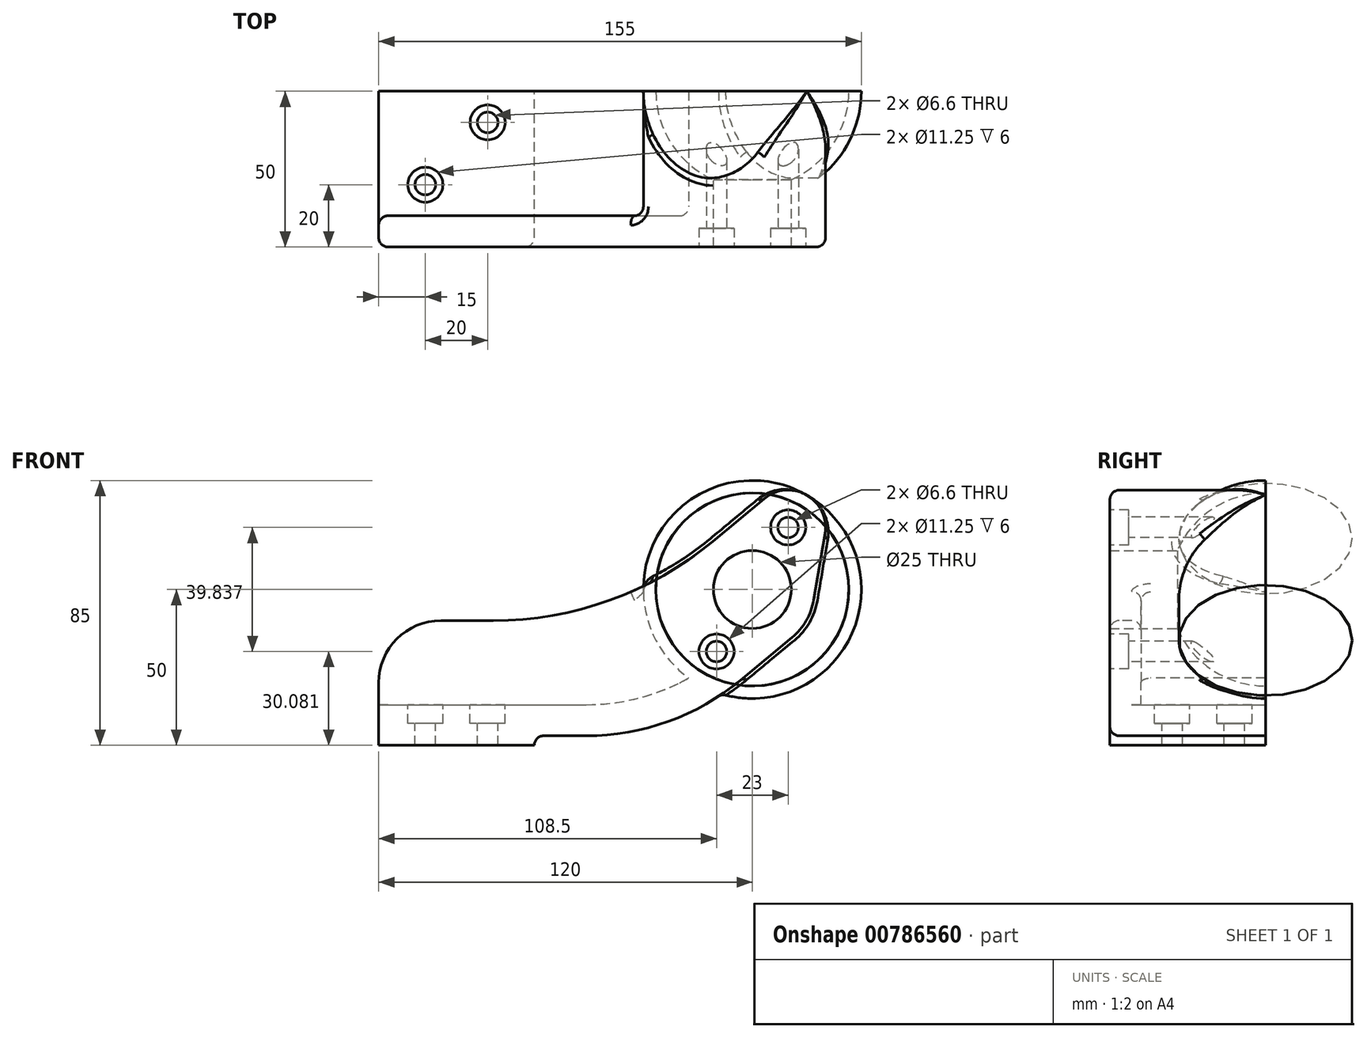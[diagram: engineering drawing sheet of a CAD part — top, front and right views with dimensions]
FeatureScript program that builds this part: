
annotation { "Feature Type Name" : "Feature", "Feature Type Description" : "" }
export const myFeature = defineFeature(function(context is Context, id is Id, definition is map)
    precondition{}
    {
        {
            var Q0;
            Q0=qCreatedBy(makeId("Front.planeOp"),FACE);
            var sketch = newSketch(context, id + "F0", { "sketchPlane" : qUnion([Q0])});
            skCircle(sketch, "E0", {"center": v(120, 50) * mm, "radius": 35 * mm});
            skCircle(sketch, "E1", {"center": v(120, 50) * mm, "radius": 12.5 * mm});
            skLineSegment(sketch, "E2", {"start": v(102.5, 19.69) * mm, "end": v(137.5, 80.31) * mm, "construction": true});
            skArc(sketch, "E3", {"start": v(122.23, 62.3) * mm, "mid": v(125.5, 59.53) * mm, "end": v(129.54, 58.08) * mm, "construction": true});
            skArc(sketch, "E4", {"start": v(96.67, 32.1) * mm, "mid": v(102.5, 19.69) * mm, "end": v(116.16, 20.84) * mm});
            skArc(sketch, "E5", {"start": v(107.24, 65.4) * mm, "mid": v(102.68, 60) * mm, "end": v(100.28, 53.35) * mm});
            skLineSegment(sketch, "E6", {"start": v(0, 0) * mm, "end": v(50, 0) * mm});
            skLineSegment(sketch, "E7", {"start": v(50, 0) * mm, "end": v(50, 3) * mm});
            skLineSegment(sketch, "E8", {"start": v(50, 3) * mm, "end": v(66.66, 3) * mm});
            skLineSegment(sketch, "E9", {"start": v(0, 0) * mm, "end": v(0, 40) * mm});
            skLineSegment(sketch, "E10", {"start": v(0, 40) * mm, "end": v(86.46, 40) * mm});
            skLineSegment(sketch, "E11", {"start": v(139.72, 46.65) * mm, "end": v(143.33, 67.9) * mm});
            skLineSegment(sketch, "E12", {"start": v(107.24, 65.4) * mm, "end": v(123.84, 79.16) * mm});
            skLineSegment(sketch, "E13", {"start": v(100.28, 53.35) * mm, "end": v(96.67, 32.1) * mm});
            skLineSegment(sketch, "E14", {"start": v(132.76, 34.6) * mm, "end": v(116.16, 20.84) * mm});
            skArc(sketch, "E15.trimOffspring", {"start": v(143.33, 67.9) * mm, "mid": v(137.5, 80.31) * mm, "end": v(123.84, 79.16) * mm});
            skArc(sketch, "E16.trimOffspring", {"start": v(117.77, 37.7) * mm, "mid": v(114.5, 40.47) * mm, "end": v(110.46, 41.92) * mm, "construction": true});
            skArc(sketch, "E17.trimOffspring", {"start": v(132.76, 34.6) * mm, "mid": v(137.32, 40) * mm, "end": v(139.72, 46.65) * mm});
            skArc(sketch, "E18", {"start": v(66.66, 3) * mm, "mid": v(92.97, 7.6) * mm, "end": v(116.16, 20.84) * mm});
            skArc(sketch, "E19.0", {"start": v(66.66, 13) * mm, "mid": v(83.84, 15.22) * mm, "end": v(99.88, 21.73) * mm});
            skLineSegment(sketch, "E20", {"start": v(0, 13) * mm, "end": v(66.66, 13) * mm});
            skSolve(sketch);
        }
        {
            var Q0;
            Q0=makeQuery(id+"F0.imprint","IMPRINT",FACE,{"disambiguationData":[TD([[makeQuery(id+"F0.imprint","IMPRINT",EDGE,{"derivedFrom":sQuery(id+"F0.wireOp",EDGE,"E5")}),-1.0]])]});
            var sketch = newSketch(context, id + "F1", { "sketchPlane" : qUnion([Q0])});
            skArc(sketch, "E21.0", {"start": v(119.02, 84.99) * mm, "mid": v(85.01, 49.02) * mm, "end": v(120.98, 15.01) * mm});
            skLineSegment(sketch, "E22", {"start": v(119.02, 84.99) * mm, "end": v(120.98, 15.01) * mm});
            skSolve(sketch);
        }
        {
            var Q0;
            Q0 = qSketchRegion(id + "F1", true);
            var Q1;
            Q1=sQuery(id+"F1.wireOp",EDGE,"E22");
            revolve(context, id + "F2", {"surfaceOperationType" : NewSurfaceOperationType.NEW, "entities" : qUnion([Q0]), "axis" : qUnion([Q1]), "revolveType" : RevolveType.ONE_DIRECTION, "oppositeDirection" : true, "angle" : 180 * degree});
        }
        {
            var Q0;
            {var subQ0=sQuery(id+"F0.wireOp",EDGE,"E19.0");var subQ1=sQuery(id+"F0.wireOp",EDGE,"E0");var subQ2=makeQuery(id+"F0.imprint","INTERSECT",VERTEX,{"derivedFrom":[subQ1,subQ0]});Q0=makeQuery(id+"F0.imprint","IMPRINT",FACE,{"disambiguationData":[TD([[makeQuery(id+"F0.imprint","IMPRINT",EDGE,{"disambiguationData":[TD([[subQ2,-1.0]])],"derivedFrom":subQ1}),1.0]])]});}
            var Q1;
            {var subQ0=sQuery(id+"F0.wireOp",EDGE,"E18");var subQ1=sQuery(id+"F0.wireOp",EDGE,"E0");var subQ2=makeQuery(id+"F0.imprint","INTERSECT",VERTEX,{"derivedFrom":[subQ1,subQ0]});Q1=makeQuery(id+"F0.imprint","IMPRINT",FACE,{"disambiguationData":[TD([[makeQuery(id+"F0.imprint","IMPRINT",EDGE,{"disambiguationData":[TD([[subQ2,1.0]])],"derivedFrom":subQ1}),1.0]])]});}
            var Q2;
            {var subQ0=sQuery(id+"F0.wireOp",EDGE,"E6");Q2=makeQuery(id+"F0.imprint","IMPRINT",FACE,{"disambiguationData":[TD([[makeQuery(id+"F0.imprint","IMPRINT",EDGE,{"derivedFrom":subQ0}),1.0]])]});}
            var Q3;
            Q3=makeQuery(id+"F0.imprint","IMPRINT",FACE,{"disambiguationData":[TD([[makeQuery(id+"F0.imprint","IMPRINT",EDGE,{"derivedFrom":sQuery(id+"F0.wireOp",EDGE,"E1")}),-1.0]])]});
            var Q4;
            Q4=makeQuery(id+"F0.imprint","IMPRINT",FACE,{"disambiguationData":[TD([[makeQuery(id+"F0.imprint","IMPRINT",EDGE,{"derivedFrom":sQuery(id+"F0.wireOp",EDGE,"E1")}),1.0]])]});
            extrude(context, id + "F3", {"entities" : qUnion([Q0, Q1, Q2, Q3, Q4]), "operationType" : NewBodyOperationType.ADD, "depth" : 50 * mm, "offsetDistance" : 25 * mm});
        }
        {
            var Q0;
            {var subQ0=sQuery(id+"F0.wireOp",EDGE,"E20");Q0=makeQuery(id+"FL2OrtGu8nAbXdU_1.boolean.opBoolean","MERGE",FACE,{"derivedFrom":[makeQuery(id+"F3.opExtrude","SWEPT_FACE",FACE,{"disambiguationData":[OSD([subQ0])]}),makeQuery(id+"FL2OrtGu8nAbXdU_1.opExtrude","SWEPT_FACE",FACE,{"disambiguationData":[OSD([sQuery(id+"F0.wireOp",EDGE,"E9"),subQ0])]})]});}
            var sketch = newSketch(context, id + "F4", { "sketchPlane" : qUnion([Q0])});
            skPoint(sketch, "E23", {"position": v(15, -30) * mm});
            skPoint(sketch, "E24", {"position": v(35, -10) * mm});
            skSolve(sketch);
        }
        {
            var Q0;
            Q0=makeQuery(id+"F3.opExtrude","CAP_FACE",FACE,{"disambiguationData":[OSD([sQuery(id+"F0.wireOp",EDGE,"E1"),sQuery(id+"F0.wireOp",EDGE,"E4"),sQuery(id+"F0.wireOp",EDGE,"E5"),sQuery(id+"F0.wireOp",EDGE,"E6"),sQuery(id+"F0.wireOp",EDGE,"E7"),sQuery(id+"F0.wireOp",EDGE,"E8"),sQuery(id+"F0.wireOp",EDGE,"E9"),sQuery(id+"F0.wireOp",EDGE,"E11"),sQuery(id+"F0.wireOp",EDGE,"E12"),sQuery(id+"F0.wireOp",EDGE,"E13"),sQuery(id+"F0.wireOp",EDGE,"E14"),sQuery(id+"F0.wireOp",EDGE,"E15.trimOffspring"),sQuery(id+"F0.wireOp",EDGE,"E17.trimOffspring"),sQuery(id+"F0.wireOp",EDGE,"E18"),sQuery(id+"F0.wireOp",EDGE,"E19.0"),sQuery(id+"F0.wireOp",EDGE,"E20")])],"isStart":false});
            var sketch = newSketch(context, id + "F5", { "sketchPlane" : qUnion([Q0])});
            skCircle(sketch, "E25", {"center": v(120, 50) * mm, "radius": 23 * mm, "construction": true});
            skLineSegment(sketch, "E26", {"start": v(108.5, 30.08) * mm, "end": v(131.5, 69.92) * mm, "construction": true});
            skSolve(sketch);
        }
        {
            var Q0;
            Q0=sQuery(id+"F4.wireOp",VERTEX,"E24");
            var Q1;
            Q1=sQuery(id+"F4.wireOp",VERTEX,"E23");
            var Q2;
            Q2=sQuery(id+"F5.wireOp",VERTEX,"E26.end");
            var Q3;
            Q3=sQuery(id+"F5.wireOp",VERTEX,"E26.start");
            var Q4;
            Q4=makeQuery(id+"F2.opRevolve","SWEPT_BODY",BODY,{"disambiguationData":[OSD([sQuery(id+"F1.wireOp",EDGE,"E21.0"),sQuery(id+"F1.wireOp",EDGE,"E22")])]});
            hole(context, id + "F6", {"style" : HoleStyle.C_BORE, "endStyle" : HoleEndStyle.THROUGH, "standardTappedOrClearance" : lookupTablePath({ "standard" : "ISO", "fit" : "Normal", "size" : "M6", "type" : "Clearance" }), "standardBlindInLast" : lookupTablePath({ "fit" : "Standard", "standard" : "ISO", "size" : "M6", "type" : "Clearance" }), "holeDiameter" : 6.6 * mm, "cBoreDiameter" : 11.25 * mm, "cBoreDepth" : 6 * mm, "majorDiameter" : 5 * mm, "isTappedThrough" : true, "tappedDepth" : 12 * mm, "tapClearance" : 3, "locations" : qUnion([Q0, Q1, Q2, Q3]), "scope" : qUnion([Q4])});
        }
        {
            var Q0;
            Q0=makeQuery(id+"FmB4rHgyCXXtYKF_1.boolean.opBoolean","MERGE",FACE,{"derivedFrom":[makeQuery(id+"F3.boolean.opBoolean","MERGE",FACE,{"derivedFrom":[makeQuery(id+"F2.opRevolve","CAP_FACE",FACE,{"disambiguationData":[OSD([sQuery(id+"F1.wireOp",EDGE,"E21.0"),sQuery(id+"F1.wireOp",EDGE,"E22")])],"isStart":true}),makeQuery(id+"F3.opExtrude","CAP_FACE",FACE,{"disambiguationData":[OSD([sQuery(id+"F0.wireOp",EDGE,"E1"),sQuery(id+"F0.wireOp",EDGE,"E4"),sQuery(id+"F0.wireOp",EDGE,"E5"),sQuery(id+"F0.wireOp",EDGE,"E6"),sQuery(id+"F0.wireOp",EDGE,"E7"),sQuery(id+"F0.wireOp",EDGE,"E8"),sQuery(id+"F0.wireOp",EDGE,"E9"),sQuery(id+"F0.wireOp",EDGE,"E11"),sQuery(id+"F0.wireOp",EDGE,"E12"),sQuery(id+"F0.wireOp",EDGE,"E13"),sQuery(id+"F0.wireOp",EDGE,"E14"),sQuery(id+"F0.wireOp",EDGE,"E15.trimOffspring"),sQuery(id+"F0.wireOp",EDGE,"E17.trimOffspring"),sQuery(id+"F0.wireOp",EDGE,"E18"),sQuery(id+"F0.wireOp",EDGE,"E19.0"),sQuery(id+"F0.wireOp",EDGE,"E20")])],"isStart":true})]}),makeQuery(id+"FmB4rHgyCXXtYKF_1.opExtrude","SWEPT_FACE",FACE,{"disambiguationData":[OSD([sQuery(id+"Fw0tHJBMQvCtHRQ_1.wireOp",EDGE,"a3YMDeG1-MOU3-Fpiz-S6uy-zRs6AQd0MLk7.left")])]})]});
            var sketch = newSketch(context, id + "F7", { "sketchPlane" : qUnion([Q0])});
            skArc(sketch, "E27.0", {"start": v(-131.95, 78.6) * mm, "mid": v(-148.6, 38.05) * mm, "end": v(-108.05, 21.4) * mm});
            skLineSegment(sketch, "E28", {"start": v(-108.05, 21.4) * mm, "end": v(-131.95, 78.6) * mm});
            skSolve(sketch);
        }
        {
            var Q0;
            Q0 = qSketchRegion(id + "F7", true);
            var Q1;
            Q1=sQuery(id+"F7.wireOp",EDGE,"E28");
            revolve(context, id + "F8", {"operationType" : NewBodyOperationType.REMOVE, "surfaceOperationType" : NewSurfaceOperationType.NEW, "entities" : qUnion([Q0]), "axis" : qUnion([Q1]), "revolveType" : RevolveType.FULL, "oppositeDirection" : true});
        }
        {
            var Q0;
            Q0=makeQuery(id+"F0.imprint","IMPRINT",FACE,{"disambiguationData":[TD([[makeQuery(id+"F0.imprint","IMPRINT",EDGE,{"derivedFrom":sQuery(id+"F0.wireOp",EDGE,"E1")}),1.0]])]});
            extrude(context, id + "F9", {"entities" : qUnion([Q0]), "operationType" : NewBodyOperationType.REMOVE, "endBound" : BoundingType.THROUGH_ALL, "depth" : 106.3 * mm, "offsetDistance" : 25 * mm});
        }
        {
            var Q0;
            Q0=makeQuery(id+"F3.opExtrude","CAP_FACE",FACE,{"disambiguationData":[OSD([sQuery(id+"F0.wireOp",EDGE,"E4"),sQuery(id+"F0.wireOp",EDGE,"E5"),sQuery(id+"F0.wireOp",EDGE,"E6"),sQuery(id+"F0.wireOp",EDGE,"E7"),sQuery(id+"F0.wireOp",EDGE,"E8"),sQuery(id+"F0.wireOp",EDGE,"E9"),sQuery(id+"F0.wireOp",EDGE,"E11"),sQuery(id+"F0.wireOp",EDGE,"E12"),sQuery(id+"F0.wireOp",EDGE,"E13"),sQuery(id+"F0.wireOp",EDGE,"E14"),sQuery(id+"F0.wireOp",EDGE,"E15.trimOffspring"),sQuery(id+"F0.wireOp",EDGE,"E17.trimOffspring"),sQuery(id+"F0.wireOp",EDGE,"E18"),sQuery(id+"F0.wireOp",EDGE,"E19.0"),sQuery(id+"F0.wireOp",EDGE,"E20")])],"isStart":false});
            var sketch = newSketch(context, id + "F10", { "sketchPlane" : qUnion([Q0])});
            skLineSegment(sketch, "E29", {"start": v(0, 13) * mm, "end": v(0, 20) * mm});
            skLineSegment(sketch, "E30", {"start": v(20, 40) * mm, "end": v(36.78, 40) * mm});
            skArc(sketch, "E31", {"start": v(36.78, 40) * mm, "mid": v(74.23, 46.54) * mm, "end": v(107.24, 65.4) * mm});
            skPoint(sketch, "E32.visualSharp", {"position": v(0, 40) * mm});
            skArc(sketch, "E32.filletArc", {"start": v(20, 40) * mm, "mid": v(5.86, 34.14) * mm, "end": v(0, 20) * mm});
            skArc(sketch, "E33.0", {"start": v(107.24, 65.4) * mm, "mid": v(102.68, 60) * mm, "end": v(100.28, 53.35) * mm});
            skLineSegment(sketch, "E33.1", {"start": v(100.28, 53.35) * mm, "end": v(96.67, 32.1) * mm});
            skArc(sketch, "E33.2", {"start": v(96.67, 32.1) * mm, "mid": v(97.04, 26.53) * mm, "end": v(99.88, 21.73) * mm});
            skArc(sketch, "E33.3", {"start": v(66.66, 13) * mm, "mid": v(83.84, 15.22) * mm, "end": v(99.88, 21.73) * mm});
            skLineSegment(sketch, "E33.4", {"start": v(0, 13) * mm, "end": v(66.66, 13) * mm});
            skSolve(sketch);
        }
        {
            var Q0;
            Q0=makeQuery(id+"F10.imprint","IMPRINT",FACE,{"disambiguationData":[TD([[makeQuery(id+"F10.imprint","IMPRINT",EDGE,{"derivedFrom":sQuery(id+"F10.wireOp",EDGE,"E29")}),-1.0]])]});
            extrude(context, id + "F11", {"entities" : qUnion([Q0]), "operationType" : NewBodyOperationType.ADD, "oppositeDirection" : true, "depth" : 10 * mm, "offsetDistance" : 25 * mm});
        }
        {
            var Q0;
            Q0=makeQuery(id+"F11.boolean.opBoolean","MERGE",FACE,{"derivedFrom":[makeQuery(id+"F3.opExtrude","CAP_FACE",FACE,{"disambiguationData":[OSD([sQuery(id+"F0.wireOp",EDGE,"E4"),sQuery(id+"F0.wireOp",EDGE,"E5"),sQuery(id+"F0.wireOp",EDGE,"E6"),sQuery(id+"F0.wireOp",EDGE,"E7"),sQuery(id+"F0.wireOp",EDGE,"E8"),sQuery(id+"F0.wireOp",EDGE,"E9"),sQuery(id+"F0.wireOp",EDGE,"E11"),sQuery(id+"F0.wireOp",EDGE,"E12"),sQuery(id+"F0.wireOp",EDGE,"E13"),sQuery(id+"F0.wireOp",EDGE,"E14"),sQuery(id+"F0.wireOp",EDGE,"E15.trimOffspring"),sQuery(id+"F0.wireOp",EDGE,"E17.trimOffspring"),sQuery(id+"F0.wireOp",EDGE,"E18"),sQuery(id+"F0.wireOp",EDGE,"E19.0"),sQuery(id+"F0.wireOp",EDGE,"E20")])],"isStart":false}),makeQuery(id+"F11.opExtrude","CAP_FACE",FACE,{"disambiguationData":[OSD([sQuery(id+"F10.wireOp",EDGE,"E29"),sQuery(id+"F10.wireOp",EDGE,"E30"),sQuery(id+"F10.wireOp",EDGE,"E31"),sQuery(id+"F10.wireOp",EDGE,"E32.filletArc"),sQuery(id+"F10.wireOp",EDGE,"E33.0"),sQuery(id+"F10.wireOp",EDGE,"E33.1"),sQuery(id+"F10.wireOp",EDGE,"E33.2"),sQuery(id+"F10.wireOp",EDGE,"E33.3"),sQuery(id+"F10.wireOp",EDGE,"E33.4")])],"isStart":true})]});
            var sketch = newSketch(context, id + "F12", { "sketchPlane" : qUnion([Q0])});
            skArc(sketch, "E34.0.0", {"start": v(85.02, 51.1) * mm, "mid": v(88.61, 34.5) * mm, "end": v(99.6, 21.57) * mm});
            skArc(sketch, "E34.0.1", {"start": v(99.88, 21.73) * mm, "mid": v(99.74, 21.65) * mm, "end": v(99.6, 21.57) * mm});
            skArc(sketch, "E34.0.2", {"start": v(99.88, 21.73) * mm, "mid": v(97.04, 26.53) * mm, "end": v(96.67, 32.1) * mm});
            skLineSegment(sketch, "E34.0.3", {"start": v(96.67, 32.1) * mm, "end": v(100.28, 53.35) * mm});
            skArc(sketch, "E34.0.4", {"start": v(107.24, 65.4) * mm, "mid": v(102.68, 60) * mm, "end": v(100.28, 53.35) * mm});
            skArc(sketch, "E35.0", {"start": v(85.02, 51.1) * mm, "mid": v(96.56, 57.58) * mm, "end": v(107.24, 65.4) * mm});
            skPoint(sketch, "E34.0.6.start.orphan", {"position": v(123.84, 79.16) * mm});
            skPoint(sketch, "E36.orphan", {"position": v(137.5, 80.31) * mm});
            skSolve(sketch);
        }
        {
            var Q0;
            Q0=makeQuery(id+"F12.imprint","IMPRINT",FACE,{"disambiguationData":[TD([[makeQuery(id+"F12.imprint","IMPRINT",EDGE,{"derivedFrom":sQuery(id+"F12.wireOp",EDGE,"E34.0.0")}),1.0]])]});
            var Q1;
            {var subQ5=sQuery(id+"F0.wireOp",EDGE,"E4");var subQ6=sQuery(id+"F1.wireOp",EDGE,"E21.0");var subQ7=makeQuery(id+"F2.opRevolve","SWEPT_FACE",FACE,{"disambiguationData":[OSD([subQ6])]});Q1=makeQuery(id+"F3.boolean.opBoolean","SPLIT",FACE,{"disambiguationData":[TD([makeQuery(id+"F3.opExtrude","SWEPT_FACE",FACE,{"disambiguationData":[OSD([subQ5])]})])],"derivedFrom":subQ7});}
            extrude(context, id + "F13", {"entities" : qUnion([Q0]), "operationType" : NewBodyOperationType.ADD, "endBound" : BoundingType.UP_TO_SURFACE, "oppositeDirection" : true, "depth" : 21.1 * mm, "endBoundEntityFace" : qUnion([Q1]), "offsetDistance" : 25 * mm});
        }
        {
            var Q0;
            Q0=makeQuery(id+"F13.opExtrude","SWEPT_EDGE",EDGE,{"disambiguationData":[OSD([sQuery(id+"F10.wireOp",EDGE,"E31"),sQuery(id+"F12.wireOp",EDGE,"E34.0.0"),sQuery(id+"F12.wireOp",EDGE,"E35.0")])]});
            var Q1;
            Q1=makeQuery(id+"F11.opExtrude","CAP_EDGE",EDGE,{"disambiguationData":[OSD([sQuery(id+"F10.wireOp",EDGE,"E31")])],"isStart":false});
            var Q2;
            Q2=makeQuery(id+"F13.boolean.opBoolean","INTERSECT",EDGE,{"derivedFrom":[makeQuery(id+"F11.opExtrude","CAP_FACE",FACE,{"disambiguationData":[OSD([sQuery(id+"F10.wireOp",EDGE,"E29"),sQuery(id+"F10.wireOp",EDGE,"E30"),sQuery(id+"F10.wireOp",EDGE,"E31"),sQuery(id+"F10.wireOp",EDGE,"E32.filletArc"),sQuery(id+"F10.wireOp",EDGE,"E33.0"),sQuery(id+"F10.wireOp",EDGE,"E33.1"),sQuery(id+"F10.wireOp",EDGE,"E33.2"),sQuery(id+"F10.wireOp",EDGE,"E33.3"),sQuery(id+"F10.wireOp",EDGE,"E33.4")])],"isStart":false}),makeQuery(id+"F13.opExtrude","SWEPT_FACE",FACE,{"disambiguationData":[OSD([sQuery(id+"F12.wireOp",EDGE,"E34.0.0")])]})]});
            var Q3;
            Q3=makeQuery(id+"F13.opExtrude","SWEPT_EDGE",EDGE,{"disambiguationData":[OSD([sQuery(id+"F12.wireOp",EDGE,"E34.0.0"),sQuery(id+"F12.wireOp",EDGE,"E34.0.1")])]});
            var Q4;
            Q4=makeQuery(id+"F11.opExtrude","CAP_EDGE",EDGE,{"disambiguationData":[OSD([sQuery(id+"F10.wireOp",EDGE,"E33.3")])],"isStart":false});
            var Q5;
            Q5=makeQuery(id+"F11.boolean.opBoolean","MERGE",EDGE,{"derivedFrom":[makeQuery(id+"F3.opExtrude","CAP_EDGE",EDGE,{"disambiguationData":[OSD([sQuery(id+"F0.wireOp",EDGE,"E9")])],"isStart":false}),makeQuery(id+"F11.opExtrude","CAP_EDGE",EDGE,{"disambiguationData":[OSD([sQuery(id+"F10.wireOp",EDGE,"E29")])],"isStart":true})]});
            var Q6;
            Q6=makeQuery(id+"F3.opExtrude","SWEPT_EDGE",EDGE,{"disambiguationData":[OSD([sQuery(id+"F0.wireOp",EDGE,"E7"),sQuery(id+"F0.wireOp",EDGE,"E8")])]});
            fillet(context, id + "F14", {"entities" : qUnion([Q0, Q1, Q2, Q3, Q4, Q5, Q6]), "radius" : 3 * mm, "tangentPropagation" : true, "allowEdgeOverflow" : false});
        }
        {
            var Q0;
            Q0=makeQuery(id+"F13.opExtrude","CAP_EDGE",EDGE,{"disambiguationData":[OSD([sQuery(id+"F12.wireOp",EDGE,"E35.0")])],"isStart":false});
            var Q1;
            Q1=makeQuery(id+"F3.boolean.opBoolean","INTERSECT",EDGE,{"disambiguationData":[OD(0.0)],"derivedFrom":[makeQuery(id+"F2.opRevolve","SWEPT_FACE",FACE,{"disambiguationData":[OSD([sQuery(id+"F1.wireOp",EDGE,"E21.0")])]}),makeQuery(id+"F3.opExtrude","SWEPT_FACE",FACE,{"disambiguationData":[OSD([sQuery(id+"F0.wireOp",EDGE,"E15.trimOffspring")])]})]});
            fillet(context, id + "F15", {"entities" : qUnion([Q0, Q1]), "radius" : 3 * mm, "tangentPropagation" : true, "allowEdgeOverflow" : false});
        }
    });
